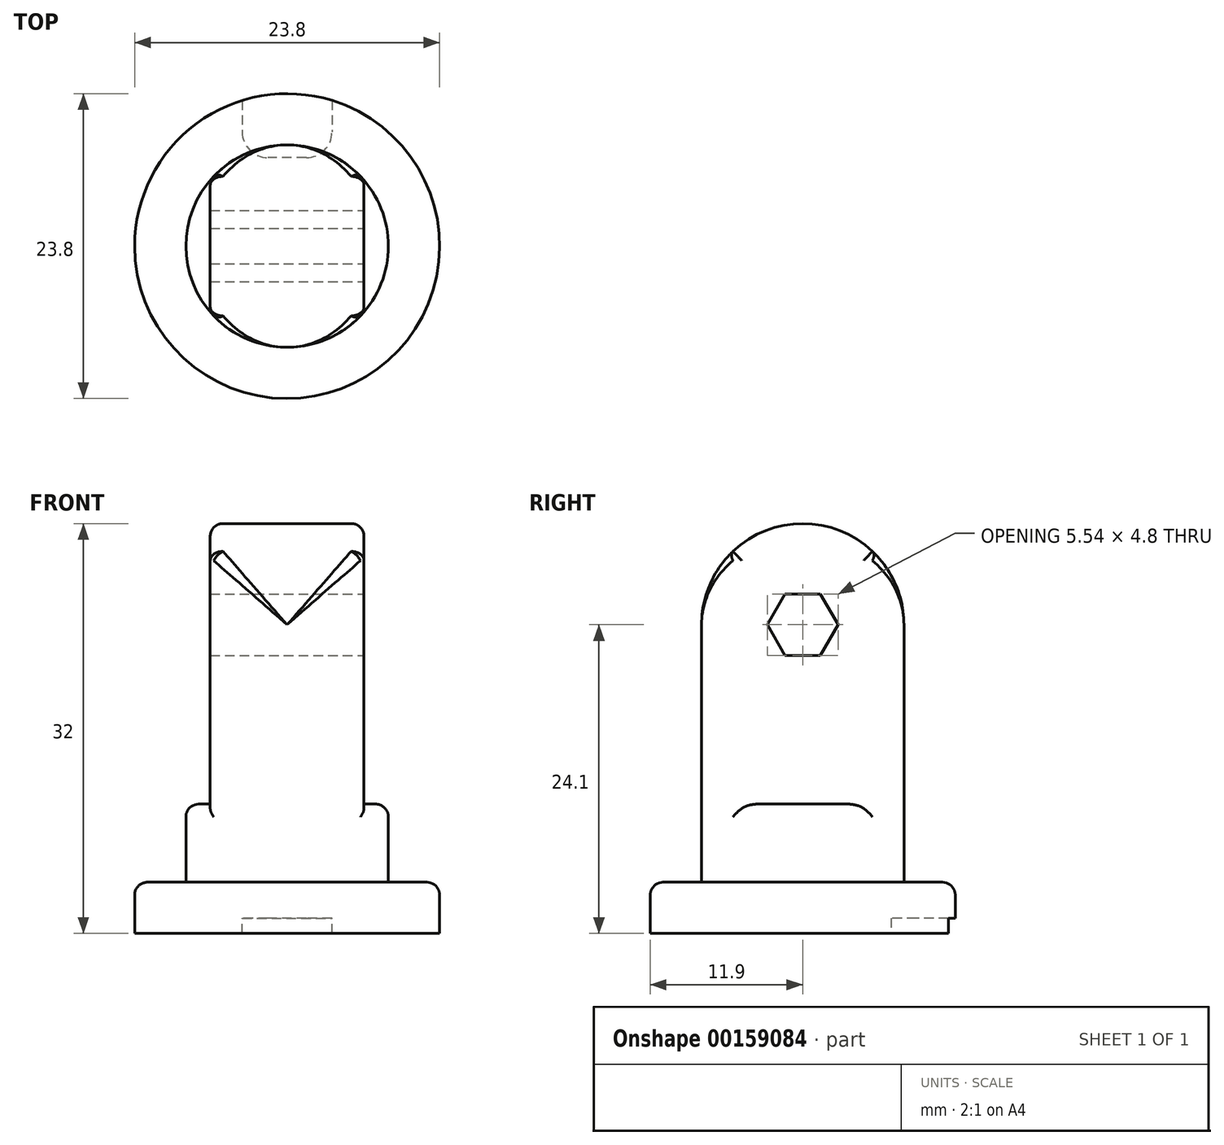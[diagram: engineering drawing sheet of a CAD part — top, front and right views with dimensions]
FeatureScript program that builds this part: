
annotation { "Feature Type Name" : "Feature", "Feature Type Description" : "" }
export const myFeature = defineFeature(function(context is Context, id is Id, definition is map)
    precondition{}
    {
        {
            var Q0;
            Q0=qCreatedBy(makeId("Right.planeOp"),FACE);
            cPlane(context, id + "F0", {"entities" : qUnion([Q0]), "cplaneType" : CPlaneType.OFFSET, "offset" : 6 * mm, "width" : 150 * mm, "height" : 150 * mm});
        }
        {
            var Q0;
            Q0=qCreatedBy(makeId("Right.planeOp"),FACE);
            cPlane(context, id + "F1", {"entities" : qUnion([Q0]), "cplaneType" : CPlaneType.OFFSET, "offset" : 6 * mm, "oppositeDirection" : true, "width" : 150 * mm, "height" : 150 * mm});
        }
        {
            var Q0;
            Q0=qCreatedBy(makeId("Right.planeOp"),FACE);
            var sketch = newSketch(context, id + "F2", { "sketchPlane" : qUnion([Q0])});
            skLineSegment(sketch, "E0", {"start": v(0, 0) * mm, "end": v(-11.9, 0) * mm});
            skLineSegment(sketch, "E1", {"start": v(-11.9, 0) * mm, "end": v(-11.9, 4) * mm});
            skLineSegment(sketch, "E2", {"start": v(-11.9, 4) * mm, "end": v(-7.9, 4) * mm});
            skLineSegment(sketch, "E3", {"start": v(-7.9, 4) * mm, "end": v(-7.9, 32) * mm});
            skLineSegment(sketch, "E4", {"start": v(-7.9, 32) * mm, "end": v(0, 32) * mm});
            skLineSegment(sketch, "E5", {"start": v(0, 32) * mm, "end": v(0, 0) * mm});
            skSolve(sketch);
        }
        {
            var Q0;
            Q0=qSketchRegion(id+"F2",true);
            var Q1;
            Q1=sQuery(id+"F2.wireOp",EDGE,"E5");
            revolve(context, id + "F3", {"entities" : qUnion([Q0]), "axis" : qUnion([Q1]), "revolveType" : RevolveType.FULL});
        }
        {
            var Q0;
            Q0=qCreatedBy(makeId("Right.planeOp"),FACE);
            var sketch = newSketch(context, id + "F4", { "sketchPlane" : qUnion([Q0])});
            skLineSegment(sketch, "E6.1", {"start": v(-7.9, 32) * mm, "end": v(7.9, 32) * mm, "construction": true});
            skLineSegment(sketch, "E7", {"start": v(7.9, 32) * mm, "end": v(7.9, 15.7) * mm, "construction": true});
            skLineSegment(sketch, "E8", {"start": v(-7.9, 15.7) * mm, "end": v(-7.9, 32) * mm, "construction": true});
            skArc(sketch, "E9", {"start": v(7.9, 24.1) * mm, "mid": v(0, 32) * mm, "end": v(-7.9, 24.1) * mm});
            skLineSegment(sketch, "E10", {"start": v(-7.9, 24.1) * mm, "end": v(-15.33, 24.1) * mm});
            skLineSegment(sketch, "E11", {"start": v(-15.33, 24.1) * mm, "end": v(-15.33, 36.8) * mm});
            skLineSegment(sketch, "E12", {"start": v(-15.33, 36.8) * mm, "end": v(13.14, 36.8) * mm});
            skLineSegment(sketch, "E13", {"start": v(13.14, 36.8) * mm, "end": v(13.14, 24.1) * mm});
            skLineSegment(sketch, "E14", {"start": v(13.14, 24.1) * mm, "end": v(7.9, 24.1) * mm});
            skCircle(sketch, "E15.cCircle", {"center": v(0, 24.1) * mm, "radius": 2.4 * mm, "construction": true});
            skLineSegment(sketch, "E15.0", {"start": v(2.77, 24.1) * mm, "end": v(1.39, 21.7) * mm});
            skLineSegment(sketch, "E15.1", {"start": v(1.39, 21.7) * mm, "end": v(-1.39, 21.7) * mm});
            skLineSegment(sketch, "E15.2", {"start": v(-1.39, 21.7) * mm, "end": v(-2.77, 24.1) * mm});
            skLineSegment(sketch, "E15.3", {"start": v(-2.77, 24.1) * mm, "end": v(-1.39, 26.5) * mm});
            skLineSegment(sketch, "E15.4", {"start": v(-1.39, 26.5) * mm, "end": v(1.39, 26.5) * mm});
            skLineSegment(sketch, "E15.5", {"start": v(1.39, 26.5) * mm, "end": v(2.77, 24.1) * mm});
            skPoint(sketch, "E15.0.midPoint", {"position": v(2.08, 22.9) * mm});
            skSolve(sketch);
        }
        {
            var Q0;
            Q0=qSketchRegion(id+"F4",true);
            extrude(context, id + "F5", {"entities" : qUnion([Q0]), "operationType" : NewBodyOperationType.REMOVE, "endBound" : BoundingType.THROUGH_ALL, "oppositeDirection" : true, "depth" : 25 * mm, "hasSecondDirection" : true, "secondDirectionBound" : BoundingType.THROUGH_ALL, "secondDirectionOppositeDirection" : false, "secondDirectionDepth" : 25 * mm});
        }
        {
            var Q0;
            Q0=qCreatedBy(id+"F0.planeOp",FACE);
            var sketch = newSketch(context, id + "F6", { "sketchPlane" : qUnion([Q0])});
            skPoint(sketch, "E16.0", {"position": v(0, 24.1) * mm});
            skLineSegment(sketch, "E17.bottom", {"start": v(9, 38.1) * mm, "end": v(-9, 38.1) * mm});
            skLineSegment(sketch, "E17.top", {"start": v(9, 10.1) * mm, "end": v(-9, 10.1) * mm});
            skLineSegment(sketch, "E17.left", {"start": v(9, 38.1) * mm, "end": v(9, 10.1) * mm});
            skLineSegment(sketch, "E17.right", {"start": v(-9, 38.1) * mm, "end": v(-9, 10.1) * mm});
            skSolve(sketch);
        }
        {
            var Q0;
            Q0=qCreatedBy(id+"F1.planeOp",FACE);
            var sketch = newSketch(context, id + "F7", { "sketchPlane" : qUnion([Q0])});
            skLineSegment(sketch, "E18.0", {"start": v(-9, 38.1) * mm, "end": v(-9, 10.1) * mm});
            skLineSegment(sketch, "E18.1", {"start": v(9, 38.1) * mm, "end": v(-9, 38.1) * mm});
            skLineSegment(sketch, "E18.2", {"start": v(9, 38.1) * mm, "end": v(9, 10.1) * mm});
            skLineSegment(sketch, "E18.3", {"start": v(9, 10.1) * mm, "end": v(-9, 10.1) * mm});
            skSolve(sketch);
        }
        {
            var Q0;
            Q0 = qSketchRegion(id + "F6", true);
            extrude(context, id + "F8", {"entities" : qUnion([Q0]), "operationType" : NewBodyOperationType.REMOVE, "depth" : 5 * mm});
        }
        {
            var Q0;
            Q0 = qSketchRegion(id + "F7", true);
            extrude(context, id + "F9", {"entities" : qUnion([Q0]), "operationType" : NewBodyOperationType.REMOVE, "oppositeDirection" : true, "depth" : 5 * mm});
        }
        {
            var Q0;
            Q0=makeQuery(id+"F3.opRevolve","SWEPT_EDGE",EDGE,{"disambiguationData":[OSD([sQuery(id+"F2.wireOp",EDGE,"E1"),sQuery(id+"F2.wireOp",EDGE,"E2")])]});
            var Q1;
            Q1=makeQuery(id+"F8.boolean.opBoolean","SPLIT",EDGE,{"disambiguationData":[OD(0.0)],"derivedFrom":makeQuery(id+"F5.boolean.opBoolean","INTERSECT",EDGE,{"disambiguationData":[OD(1.0)],"derivedFrom":[makeQuery(id+"F3.opRevolve","SWEPT_FACE",FACE,{"disambiguationData":[OSD([sQuery(id+"F2.wireOp",EDGE,"E3")])]}),makeQuery(id+"F5.opExtrude","SWEPT_FACE",FACE,{"disambiguationData":[OSD([sQuery(id+"F4.wireOp",EDGE,"E9")])]})]})});
            var Q2;
            Q2=makeQuery(id+"F8.boolean.opBoolean","SPLIT",EDGE,{"disambiguationData":[OD(1.0)],"derivedFrom":makeQuery(id+"F5.boolean.opBoolean","INTERSECT",EDGE,{"disambiguationData":[OD(1.0)],"derivedFrom":[makeQuery(id+"F3.opRevolve","SWEPT_FACE",FACE,{"disambiguationData":[OSD([sQuery(id+"F2.wireOp",EDGE,"E3")])]}),makeQuery(id+"F5.opExtrude","SWEPT_FACE",FACE,{"disambiguationData":[OSD([sQuery(id+"F4.wireOp",EDGE,"E9")])]})]})});
            var Q3;
            Q3=makeQuery(id+"F9.boolean.opBoolean","SPLIT",EDGE,{"disambiguationData":[OD(0.0)],"derivedFrom":makeQuery(id+"F5.boolean.opBoolean","INTERSECT",EDGE,{"disambiguationData":[OD(0.0)],"derivedFrom":[makeQuery(id+"F3.opRevolve","SWEPT_FACE",FACE,{"disambiguationData":[OSD([sQuery(id+"F2.wireOp",EDGE,"E3")])]}),makeQuery(id+"F5.opExtrude","SWEPT_FACE",FACE,{"disambiguationData":[OSD([sQuery(id+"F4.wireOp",EDGE,"E9")])]})]})});
            var Q4;
            Q4=makeQuery(id+"F9.boolean.opBoolean","SPLIT",EDGE,{"disambiguationData":[OD(1.0)],"derivedFrom":makeQuery(id+"F5.boolean.opBoolean","INTERSECT",EDGE,{"disambiguationData":[OD(0.0)],"derivedFrom":[makeQuery(id+"F3.opRevolve","SWEPT_FACE",FACE,{"disambiguationData":[OSD([sQuery(id+"F2.wireOp",EDGE,"E3")])]}),makeQuery(id+"F5.opExtrude","SWEPT_FACE",FACE,{"disambiguationData":[OSD([sQuery(id+"F4.wireOp",EDGE,"E9")])]})]})});
            var Q5;
            Q5=makeQuery(id+"F8.boolean.opBoolean","INTERSECT",EDGE,{"disambiguationData":[OD(0.0)],"derivedFrom":[makeQuery(id+"F3.opRevolve","SWEPT_FACE",FACE,{"disambiguationData":[OSD([sQuery(id+"F2.wireOp",EDGE,"E3")])]}),makeQuery(id+"F8.opExtrude","CAP_FACE",FACE,{"disambiguationData":[OSD([sQuery(id+"F6.wireOp",EDGE,"E17.bottom"),sQuery(id+"F6.wireOp",EDGE,"E17.top"),sQuery(id+"F6.wireOp",EDGE,"E17.left"),sQuery(id+"F6.wireOp",EDGE,"E17.right")])],"isStart":true})]});
            var Q6;
            Q6=makeQuery(id+"F8.boolean.opBoolean","INTERSECT",EDGE,{"derivedFrom":[makeQuery(id+"F3.opRevolve","SWEPT_FACE",FACE,{"disambiguationData":[OSD([sQuery(id+"F2.wireOp",EDGE,"E3")])]}),makeQuery(id+"F8.opExtrude","SWEPT_FACE",FACE,{"disambiguationData":[OSD([sQuery(id+"F6.wireOp",EDGE,"E17.top")])]})]});
            var Q7;
            Q7=makeQuery(id+"F8.boolean.opBoolean","INTERSECT",EDGE,{"disambiguationData":[OD(1.0)],"derivedFrom":[makeQuery(id+"F3.opRevolve","SWEPT_FACE",FACE,{"disambiguationData":[OSD([sQuery(id+"F2.wireOp",EDGE,"E3")])]}),makeQuery(id+"F8.opExtrude","CAP_FACE",FACE,{"disambiguationData":[OSD([sQuery(id+"F6.wireOp",EDGE,"E17.bottom"),sQuery(id+"F6.wireOp",EDGE,"E17.top"),sQuery(id+"F6.wireOp",EDGE,"E17.left"),sQuery(id+"F6.wireOp",EDGE,"E17.right")])],"isStart":true})]});
            var Q8;
            Q8=makeQuery(id+"F9.boolean.opBoolean","INTERSECT",EDGE,{"disambiguationData":[OD(0.0)],"derivedFrom":[makeQuery(id+"F3.opRevolve","SWEPT_FACE",FACE,{"disambiguationData":[OSD([sQuery(id+"F2.wireOp",EDGE,"E3")])]}),makeQuery(id+"F9.opExtrude","CAP_FACE",FACE,{"disambiguationData":[OSD([sQuery(id+"F7.wireOp",EDGE,"E18.0"),sQuery(id+"F7.wireOp",EDGE,"E18.1"),sQuery(id+"F7.wireOp",EDGE,"E18.2"),sQuery(id+"F7.wireOp",EDGE,"E18.3")])],"isStart":true})]});
            var Q9;
            Q9=makeQuery(id+"F9.boolean.opBoolean","INTERSECT",EDGE,{"derivedFrom":[makeQuery(id+"F3.opRevolve","SWEPT_FACE",FACE,{"disambiguationData":[OSD([sQuery(id+"F2.wireOp",EDGE,"E3")])]}),makeQuery(id+"F9.opExtrude","SWEPT_FACE",FACE,{"disambiguationData":[OSD([sQuery(id+"F7.wireOp",EDGE,"E18.3")])]})]});
            var Q10;
            Q10=makeQuery(id+"F9.boolean.opBoolean","INTERSECT",EDGE,{"disambiguationData":[OD(1.0)],"derivedFrom":[makeQuery(id+"F3.opRevolve","SWEPT_FACE",FACE,{"disambiguationData":[OSD([sQuery(id+"F2.wireOp",EDGE,"E3")])]}),makeQuery(id+"F9.opExtrude","CAP_FACE",FACE,{"disambiguationData":[OSD([sQuery(id+"F7.wireOp",EDGE,"E18.0"),sQuery(id+"F7.wireOp",EDGE,"E18.1"),sQuery(id+"F7.wireOp",EDGE,"E18.2"),sQuery(id+"F7.wireOp",EDGE,"E18.3")])],"isStart":true})]});
            var Q11;
            Q11=makeQuery(id+"F9.boolean.opBoolean","INTERSECT",EDGE,{"derivedFrom":[makeQuery(id+"F5.boolean.opBoolean","COPY",FACE,{"derivedFrom":makeQuery(id+"F5.opExtrude","SWEPT_FACE",FACE,{"disambiguationData":[OSD([sQuery(id+"F4.wireOp",EDGE,"E9")])]})}),makeQuery(id+"F9.opExtrude","CAP_FACE",FACE,{"disambiguationData":[OSD([sQuery(id+"F7.wireOp",EDGE,"E18.0"),sQuery(id+"F7.wireOp",EDGE,"E18.1"),sQuery(id+"F7.wireOp",EDGE,"E18.2"),sQuery(id+"F7.wireOp",EDGE,"E18.3")])],"isStart":true})]});
            var Q12;
            Q12=makeQuery(id+"F8.boolean.opBoolean","INTERSECT",EDGE,{"derivedFrom":[makeQuery(id+"F5.boolean.opBoolean","COPY",FACE,{"derivedFrom":makeQuery(id+"F5.opExtrude","SWEPT_FACE",FACE,{"disambiguationData":[OSD([sQuery(id+"F4.wireOp",EDGE,"E9")])]})}),makeQuery(id+"F8.opExtrude","CAP_FACE",FACE,{"disambiguationData":[OSD([sQuery(id+"F6.wireOp",EDGE,"E17.bottom"),sQuery(id+"F6.wireOp",EDGE,"E17.top"),sQuery(id+"F6.wireOp",EDGE,"E17.left"),sQuery(id+"F6.wireOp",EDGE,"E17.right")])],"isStart":true})]});
            fillet(context, id + "F10", {"entities" : qUnion([Q0, Q1, Q2, Q3, Q4, Q5, Q6, Q7, Q8, Q9, Q10, Q11, Q12]), "radius" : 1 * mm, "tangentPropagation" : true, "allowEdgeOverflow" : false});
        }
        {
            var Q0;
            Q0=makeQuery(id+"F3.opRevolve","SWEPT_FACE",FACE,{"disambiguationData":[OSD([sQuery(id+"F2.wireOp",EDGE,"E0")])]});
            var sketch = newSketch(context, id + "F11", { "sketchPlane" : qUnion([Q0])});
            skLineSegment(sketch, "E19.bottom", {"start": v(3.5, -16.9) * mm, "end": v(-3.5, -16.9) * mm});
            skLineSegment(sketch, "E19.top", {"start": v(1.5, -6.9) * mm, "end": v(-1.5, -6.9) * mm});
            skLineSegment(sketch, "E19.left", {"start": v(3.5, -16.9) * mm, "end": v(3.5, -8.9) * mm});
            skLineSegment(sketch, "E19.right", {"start": v(-3.5, -16.9) * mm, "end": v(-3.5, -8.9) * mm});
            skPoint(sketch, "E19.middle", {"position": v(0, -11.9) * mm});
            skPoint(sketch, "E20.visualSharp", {"position": v(3.5, -6.9) * mm});
            skArc(sketch, "E20.filletArc", {"start": v(3.5, -8.9) * mm, "mid": v(2.91, -7.49) * mm, "end": v(1.5, -6.9) * mm});
            skPoint(sketch, "E21.visualSharp", {"position": v(-3.5, -6.9) * mm});
            skArc(sketch, "E21.filletArc", {"start": v(-1.5, -6.9) * mm, "mid": v(-2.91, -7.49) * mm, "end": v(-3.5, -8.9) * mm});
            skSolve(sketch);
        }
        {
            var Q0;
            Q0 = qSketchRegion(id + "F11", true);
            extrude(context, id + "F12", {"entities" : qUnion([Q0]), "operationType" : NewBodyOperationType.REMOVE, "oppositeDirection" : true, "depth" : 1.2 * mm});
        }
    });
